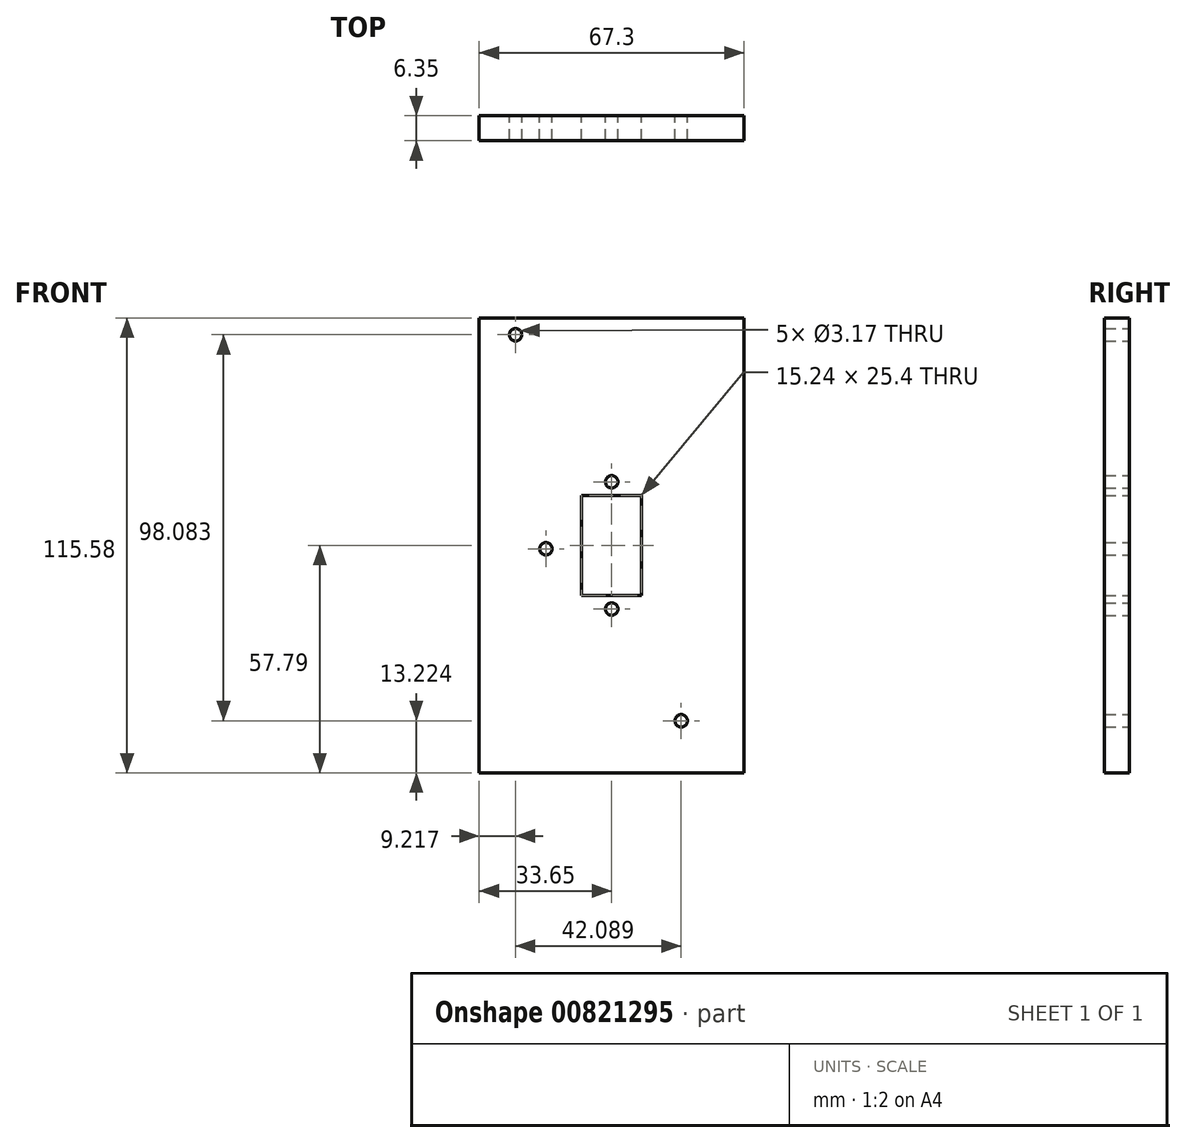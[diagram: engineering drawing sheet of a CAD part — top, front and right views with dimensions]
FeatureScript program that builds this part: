
annotation { "Feature Type Name" : "Feature", "Feature Type Description" : "" }
export const myFeature = defineFeature(function(context is Context, id is Id, definition is map)
    precondition{}
    {
        {
            var Q0;
            Q0=qCreatedBy(makeId("Front.planeOp"),FACE);
            var sketch = newSketch(context, id + "F0", { "sketchPlane" : qUnion([Q0])});
            skLineSegment(sketch, "E0.bottom", {"start": v(33.66, -57.79) * mm, "end": v(-33.66, -57.79) * mm});
            skLineSegment(sketch, "E0.top", {"start": v(33.66, 57.79) * mm, "end": v(-33.66, 57.79) * mm});
            skLineSegment(sketch, "E0.left", {"start": v(33.65, -57.79) * mm, "end": v(33.66, 57.79) * mm});
            skLineSegment(sketch, "E0.right", {"start": v(-33.66, -57.79) * mm, "end": v(-33.66, 57.78) * mm});
            skPoint(sketch, "E0.middle", {"position": v(0, 0) * mm});
            skCircle(sketch, "E1", {"center": v(-16.72, -0.85) * mm, "radius": 1.59 * mm});
            skCircle(sketch, "E2", {"center": v(-24.43, 53.52) * mm, "radius": 1.59 * mm});
            skCircle(sketch, "E3", {"center": v(17.66, -44.57) * mm, "radius": 1.59 * mm});
            skLineSegment(sketch, "E4.bottom", {"start": v(7.62, -12.7) * mm, "end": v(-7.62, -12.7) * mm});
            skLineSegment(sketch, "E4.top", {"start": v(7.62, 12.7) * mm, "end": v(-7.62, 12.7) * mm});
            skLineSegment(sketch, "E4.left", {"start": v(7.62, -12.7) * mm, "end": v(7.62, 12.7) * mm});
            skLineSegment(sketch, "E4.right", {"start": v(-7.62, -12.7) * mm, "end": v(-7.62, 12.7) * mm});
            skCircle(sketch, "E5", {"center": v(0, 16.16) * mm, "radius": 1.59 * mm});
            skCircle(sketch, "E6", {"center": v(0, -16.17) * mm, "radius": 1.59 * mm});
            skSolve(sketch);
        }
        {
            var Q0;
            Q0 = qSketchRegion(id + "F0", true);
            extrude(context, id + "F1", {"entities" : qUnion([Q0]), "depth" : 6.35 * mm, "offsetDistance" : 25.4 * mm});
        }
    });
